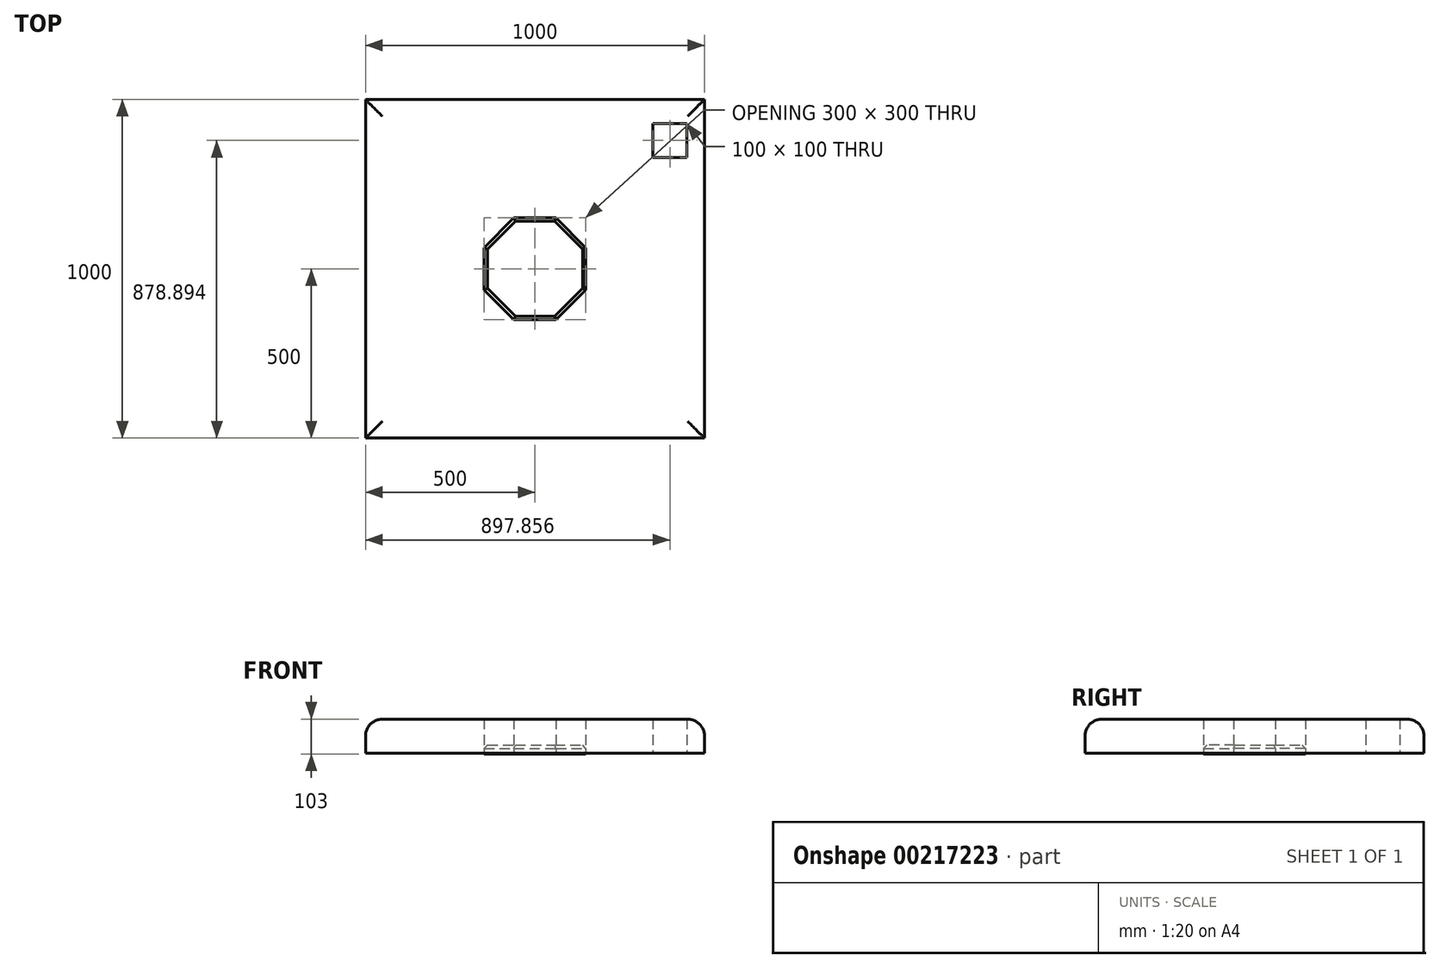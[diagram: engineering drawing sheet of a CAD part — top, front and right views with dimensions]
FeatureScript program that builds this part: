
annotation { "Feature Type Name" : "Feature", "Feature Type Description" : "" }
export const myFeature = defineFeature(function(context is Context, id is Id, definition is map)
    precondition{}
    {
        {
            var Q0;
            Q0=qCreatedBy(makeId("Top.planeOp"),FACE);
            var sketch = newSketch(context, id + "F0", { "sketchPlane" : qUnion([Q0])});
            skLineSegment(sketch, "E0.bottom", {"start": v(-500, 500) * mm, "end": v(500, 500) * mm});
            skLineSegment(sketch, "E0.top", {"start": v(-500, -500) * mm, "end": v(500, -500) * mm});
            skLineSegment(sketch, "E0.left", {"start": v(-500, 500) * mm, "end": v(-500, -500) * mm});
            skLineSegment(sketch, "E0.right", {"start": v(500, 500) * mm, "end": v(500, -500) * mm});
            skPoint(sketch, "E0.middle", {"position": v(0, 0) * mm});
            skCircle(sketch, "E1.cCircle", {"center": v(0, 0) * mm, "radius": 150 * mm, "construction": true});
            skLineSegment(sketch, "E1.0", {"start": v(62.13, -150) * mm, "end": v(-62.13, -150) * mm});
            skLineSegment(sketch, "E1.1", {"start": v(-62.13, -150) * mm, "end": v(-150, -62.13) * mm});
            skLineSegment(sketch, "E1.2", {"start": v(-150, -62.13) * mm, "end": v(-150, 62.13) * mm});
            skLineSegment(sketch, "E1.3", {"start": v(-150, 62.13) * mm, "end": v(-62.13, 150) * mm});
            skLineSegment(sketch, "E1.4", {"start": v(-62.13, 150) * mm, "end": v(62.13, 150) * mm});
            skLineSegment(sketch, "E1.5", {"start": v(62.13, 150) * mm, "end": v(150, 62.13) * mm});
            skLineSegment(sketch, "E1.6", {"start": v(150, 62.13) * mm, "end": v(150, -62.13) * mm});
            skLineSegment(sketch, "E1.7", {"start": v(150, -62.13) * mm, "end": v(62.13, -150) * mm});
            skPoint(sketch, "E1.0.midPoint", {"position": v(0, -150) * mm});
            skLineSegment(sketch, "E2.bottom", {"start": v(347.86, 428.9) * mm, "end": v(447.86, 428.9) * mm});
            skLineSegment(sketch, "E2.top", {"start": v(347.86, 328.9) * mm, "end": v(447.86, 328.9) * mm});
            skLineSegment(sketch, "E2.left", {"start": v(347.86, 428.9) * mm, "end": v(347.86, 328.9) * mm});
            skLineSegment(sketch, "E2.right", {"start": v(447.86, 428.9) * mm, "end": v(447.86, 328.9) * mm});
            skSolve(sketch);
        }
        {
            var Q0;
            Q0=makeQuery(id+"F0.imprint","IMPRINT",FACE,{"disambiguationData":[TD([[makeQuery(id+"F0.imprint","IMPRINT",EDGE,{"derivedFrom":sQuery(id+"F0.wireOp",EDGE,"E0.bottom")}),-1.0]])]});
            extrude(context, id + "F1", {"entities" : qUnion([Q0]), "depth" : 100 * mm});
        }
        {
            var Q0;
            Q0=makeQuery(id+"F1.opExtrude","CAP_EDGE",EDGE,{"disambiguationData":[OSD([sQuery(id+"F0.wireOp",EDGE,"E0.top")])],"isStart":false});
            var Q1;
            Q1=makeQuery(id+"F1.opExtrude","CAP_EDGE",EDGE,{"disambiguationData":[OSD([sQuery(id+"F0.wireOp",EDGE,"E0.right")])],"isStart":false});
            var Q2;
            Q2=makeQuery(id+"F1.opExtrude","CAP_EDGE",EDGE,{"disambiguationData":[OSD([sQuery(id+"F0.wireOp",EDGE,"E0.bottom")])],"isStart":false});
            var Q3;
            Q3=makeQuery(id+"F1.opExtrude","CAP_EDGE",EDGE,{"disambiguationData":[OSD([sQuery(id+"F0.wireOp",EDGE,"E0.left")])],"isStart":false});
            fillet(context, id + "F2", {"entities" : qUnion([Q0, Q1, Q2, Q3]), "radius" : 50 * mm, "tangentPropagation" : true, "allowEdgeOverflow" : false});
        }
        {
            var Q0;
            Q0=makeQuery(id+"F1.opExtrude","CAP_FACE",FACE,{"disambiguationData":[OSD([sQuery(id+"F0.wireOp",EDGE,"E0.bottom"),sQuery(id+"F0.wireOp",EDGE,"E0.top"),sQuery(id+"F0.wireOp",EDGE,"E0.left"),sQuery(id+"F0.wireOp",EDGE,"E0.right"),sQuery(id+"F0.wireOp",EDGE,"E1.0"),sQuery(id+"F0.wireOp",EDGE,"E1.1"),sQuery(id+"F0.wireOp",EDGE,"E1.2"),sQuery(id+"F0.wireOp",EDGE,"E1.3"),sQuery(id+"F0.wireOp",EDGE,"E1.4"),sQuery(id+"F0.wireOp",EDGE,"E1.5"),sQuery(id+"F0.wireOp",EDGE,"E1.6"),sQuery(id+"F0.wireOp",EDGE,"E1.7"),sQuery(id+"F0.wireOp",EDGE,"E2.bottom"),sQuery(id+"F0.wireOp",EDGE,"E2.top"),sQuery(id+"F0.wireOp",EDGE,"E2.left"),sQuery(id+"F0.wireOp",EDGE,"E2.right")])],"isStart":true});
            var sketch = newSketch(context, id + "F3", { "sketchPlane" : qUnion([Q0])});
            skLineSegment(sketch, "E3.bottom", {"start": v(-360.52, -394.95) * mm, "end": v(-433.2, -394.95) * mm});
            skLineSegment(sketch, "E3.top", {"start": v(-360.52, -450.4) * mm, "end": v(-433.2, -450.4) * mm});
            skLineSegment(sketch, "E3.left", {"start": v(-360.52, -394.95) * mm, "end": v(-360.52, -450.4) * mm});
            skLineSegment(sketch, "E3.right", {"start": v(-433.2, -394.95) * mm, "end": v(-433.2, -450.4) * mm});
            skLineSegment(sketch, "E4.bottom", {"start": v(-433.2, 414.07) * mm, "end": v(-356.7, 414.07) * mm});
            skLineSegment(sketch, "E4.top", {"start": v(-433.2, 347.13) * mm, "end": v(-356.7, 347.13) * mm});
            skLineSegment(sketch, "E4.left", {"start": v(-433.2, 414.07) * mm, "end": v(-433.2, 347.13) * mm});
            skLineSegment(sketch, "E4.right", {"start": v(-356.7, 414.07) * mm, "end": v(-356.7, 347.13) * mm});
            skCircle(sketch, "E5.cCircle", {"center": v(0, 0) * mm, "radius": 150 * mm, "construction": true});
            skLineSegment(sketch, "E5.0", {"start": v(-62.13, -150) * mm, "end": v(-150, -62.13) * mm});
            skLineSegment(sketch, "E5.1", {"start": v(-150, -62.13) * mm, "end": v(-150, 62.13) * mm});
            skLineSegment(sketch, "E5.2", {"start": v(-150, 62.13) * mm, "end": v(-62.13, 150) * mm});
            skLineSegment(sketch, "E5.3", {"start": v(-62.13, 150) * mm, "end": v(62.13, 150) * mm});
            skLineSegment(sketch, "E5.4", {"start": v(62.13, 150) * mm, "end": v(150, 62.13) * mm});
            skLineSegment(sketch, "E5.5", {"start": v(150, 62.13) * mm, "end": v(150, -62.13) * mm});
            skLineSegment(sketch, "E5.6", {"start": v(150, -62.13) * mm, "end": v(62.13, -150) * mm});
            skLineSegment(sketch, "E5.7", {"start": v(62.13, -150) * mm, "end": v(-62.13, -150) * mm});
            skPoint(sketch, "E5.0.midPoint", {"position": v(-106.07, -106.07) * mm});
            skSolve(sketch);
        }
        {
            var Q0;
            Q0=makeQuery(id+"F3.imprint","IMPRINT",FACE,{"disambiguationData":[TD([[makeQuery(id+"F3.imprint","IMPRINT",EDGE,{"derivedFrom":sQuery(id+"F3.wireOp",EDGE,"E5.0")}),1.0]])]});
            extrude(context, id + "F4", {"entities" : qUnion([Q0]), "depth" : 3 * mm});
        }
        {
            var Q0;
            Q0=makeQuery(id+"F4.opExtrude","CAP_FACE",FACE,{"disambiguationData":[OSD([sQuery(id+"F3.wireOp",EDGE,"E5.0"),sQuery(id+"F3.wireOp",EDGE,"E5.1"),sQuery(id+"F3.wireOp",EDGE,"E5.2"),sQuery(id+"F3.wireOp",EDGE,"E5.3"),sQuery(id+"F3.wireOp",EDGE,"E5.4"),sQuery(id+"F3.wireOp",EDGE,"E5.5"),sQuery(id+"F3.wireOp",EDGE,"E5.6"),sQuery(id+"F3.wireOp",EDGE,"E5.7")])],"isStart":true});
            extrude(context, id + "F5", {"entities" : qUnion([Q0]), "depth" : 24 * mm});
        }
        {
            var Q0;
            Q0=makeQuery(id+"F5.opExtrude","CAP_FACE",FACE,{"disambiguationData":[OSD([sQuery(id+"F3.wireOp",EDGE,"E5.0"),sQuery(id+"F3.wireOp",EDGE,"E5.1"),sQuery(id+"F3.wireOp",EDGE,"E5.2"),sQuery(id+"F3.wireOp",EDGE,"E5.3"),sQuery(id+"F3.wireOp",EDGE,"E5.4"),sQuery(id+"F3.wireOp",EDGE,"E5.5"),sQuery(id+"F3.wireOp",EDGE,"E5.6"),sQuery(id+"F3.wireOp",EDGE,"E5.7")])],"isStart":false});
            chamfer(context, id + "F6", {"entities" : qUnion([Q0]), "width" : 10 * mm, "tangentPropagation" : true});
        }
        {
            var Q0;
            Q0=makeQuery(id+"F1.opExtrude","CAP_FACE",FACE,{"disambiguationData":[OSD([sQuery(id+"F0.wireOp",EDGE,"E0.bottom"),sQuery(id+"F0.wireOp",EDGE,"E0.top"),sQuery(id+"F0.wireOp",EDGE,"E0.left"),sQuery(id+"F0.wireOp",EDGE,"E0.right"),sQuery(id+"F0.wireOp",EDGE,"E1.0"),sQuery(id+"F0.wireOp",EDGE,"E1.1"),sQuery(id+"F0.wireOp",EDGE,"E1.2"),sQuery(id+"F0.wireOp",EDGE,"E1.3"),sQuery(id+"F0.wireOp",EDGE,"E1.4"),sQuery(id+"F0.wireOp",EDGE,"E1.5"),sQuery(id+"F0.wireOp",EDGE,"E1.6"),sQuery(id+"F0.wireOp",EDGE,"E1.7"),sQuery(id+"F0.wireOp",EDGE,"E2.bottom"),sQuery(id+"F0.wireOp",EDGE,"E2.top"),sQuery(id+"F0.wireOp",EDGE,"E2.left"),sQuery(id+"F0.wireOp",EDGE,"E2.right")])],"isStart":true});
            var sketch = newSketch(context, id + "F7", { "sketchPlane" : qUnion([Q0])});
            skLineSegment(sketch, "E6.bottom", {"start": v(-366.26, 379.64) * mm, "end": v(-459.97, 379.64) * mm});
            skLineSegment(sketch, "E6.top", {"start": v(-366.26, 456.15) * mm, "end": v(-459.97, 456.15) * mm});
            skLineSegment(sketch, "E6.left", {"start": v(-366.26, 379.64) * mm, "end": v(-366.26, 456.15) * mm});
            skLineSegment(sketch, "E6.right", {"start": v(-459.97, 379.64) * mm, "end": v(-459.97, 456.15) * mm});
            skLineSegment(sketch, "E7.bottom", {"start": v(-439.2, -393.09) * mm, "end": v(-349.44, -393.09) * mm});
            skLineSegment(sketch, "E7.top", {"start": v(-439.2, -467.57) * mm, "end": v(-349.44, -467.57) * mm});
            skLineSegment(sketch, "E7.left", {"start": v(-439.2, -393.09) * mm, "end": v(-439.2, -467.57) * mm});
            skLineSegment(sketch, "E7.right", {"start": v(-349.44, -393.09) * mm, "end": v(-349.44, -467.57) * mm});
            skSolve(sketch);
        }
    });
